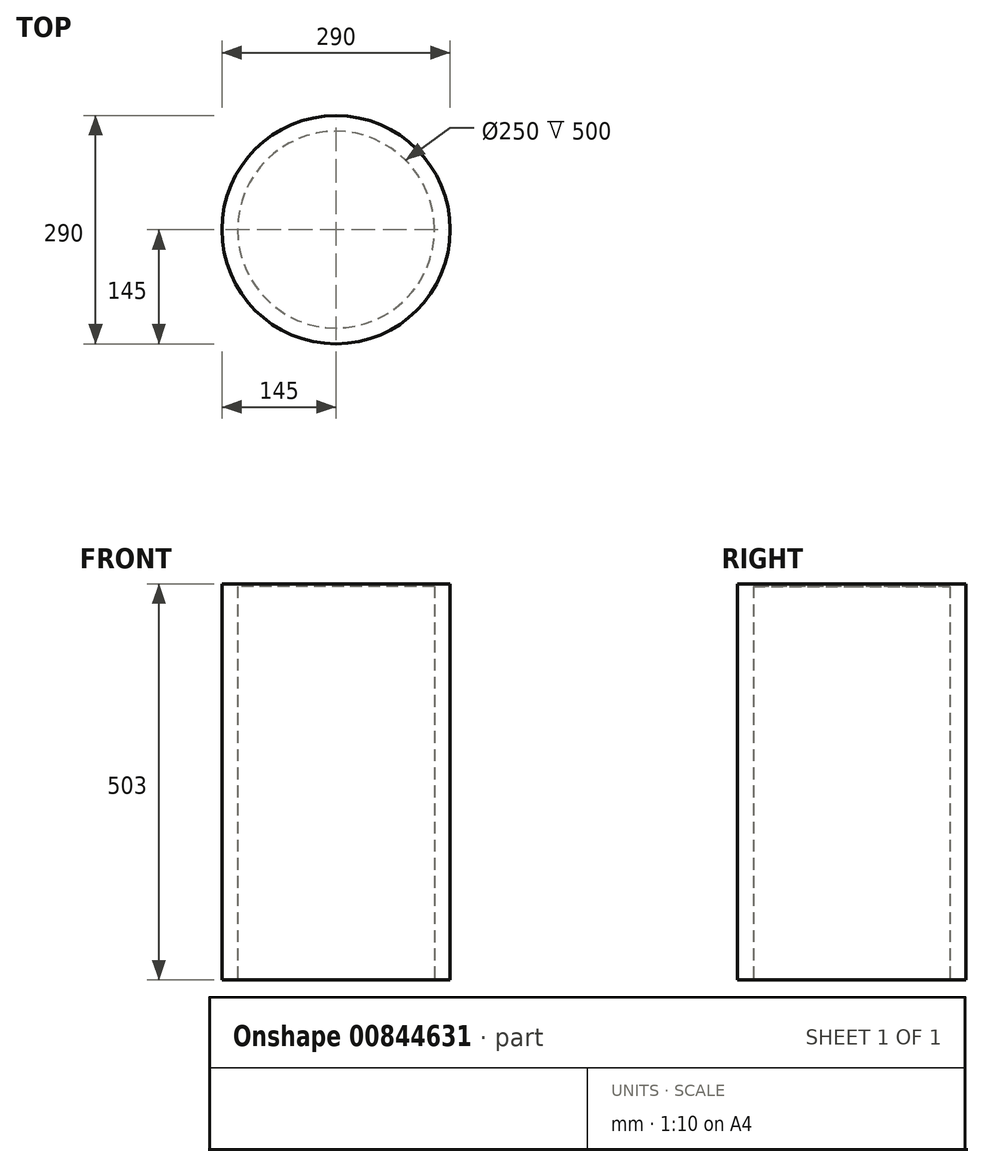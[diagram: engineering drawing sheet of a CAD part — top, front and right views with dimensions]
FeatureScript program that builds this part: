
annotation { "Feature Type Name" : "Feature", "Feature Type Description" : "" }
export const myFeature = defineFeature(function(context is Context, id is Id, definition is map)
    precondition{}
    {
        {
            var Q0;
            Q0=qCreatedBy(makeId("Top.planeOp"),FACE);
            var sketch = newSketch(context, id + "F0", { "sketchPlane" : qUnion([Q0])});
            skCircle(sketch, "E0", {"center": v(0, 0) * mm, "radius": 145 * mm});
            skCircle(sketch, "E1.0", {"center": v(0, 0) * mm, "radius": 125 * mm});
            skSolve(sketch);
        }
        {
            var Q0;
            Q0=makeQuery(id+"F0.imprint","IMPRINT",FACE,{"disambiguationData":[TD([[makeQuery(id+"F0.imprint","IMPRINT",EDGE,{"derivedFrom":sQuery(id+"F0.wireOp",EDGE,"E0")}),1.0]])]});
            extrude(context, id + "F1", {"entities" : qUnion([Q0]), "depth" : 500 * mm, "offsetDistance" : 25 * mm});
        }
        {
            var Q0;
            Q0=makeQuery(id+"F1.opExtrude","CAP_FACE",FACE,{"disambiguationData":[OSD([sQuery(id+"F0.wireOp",EDGE,"E0"),sQuery(id+"F0.wireOp",EDGE,"E1.0")])],"isStart":false});
            var sketch = newSketch(context, id + "F2", { "sketchPlane" : qUnion([Q0])});
            skSolve(sketch);
        }
        {
            var Q0;
            Q0=makeQuery(id+"F2.imprint","IMPRINT",FACE,{"disambiguationData":[TD([[makeQuery(id+"F2.imprint","IMPRINT",EDGE,{"derivedFrom":makeQuery(id+"F1.opExtrude","CAP_EDGE",EDGE,{"disambiguationData":[OSD([sQuery(id+"F0.wireOp",EDGE,"E0")])],"isStart":false})}),1.0]])]});
            var Q1;
            Q1=makeQuery(id+"F2.imprint","IMPRINT",FACE,{"disambiguationData":[TD([[makeQuery(id+"F2.imprint","IMPRINT",EDGE,{"derivedFrom":makeQuery(id+"F1.opExtrude","CAP_EDGE",EDGE,{"disambiguationData":[OSD([sQuery(id+"F0.wireOp",EDGE,"E1.0")])],"isStart":false})}),1.0]])]});
            extrude(context, id + "F3", {"entities" : qUnion([Q0, Q1]), "operationType" : NewBodyOperationType.ADD, "depth" : 3 * mm, "offsetDistance" : 25 * mm});
        }
    });
